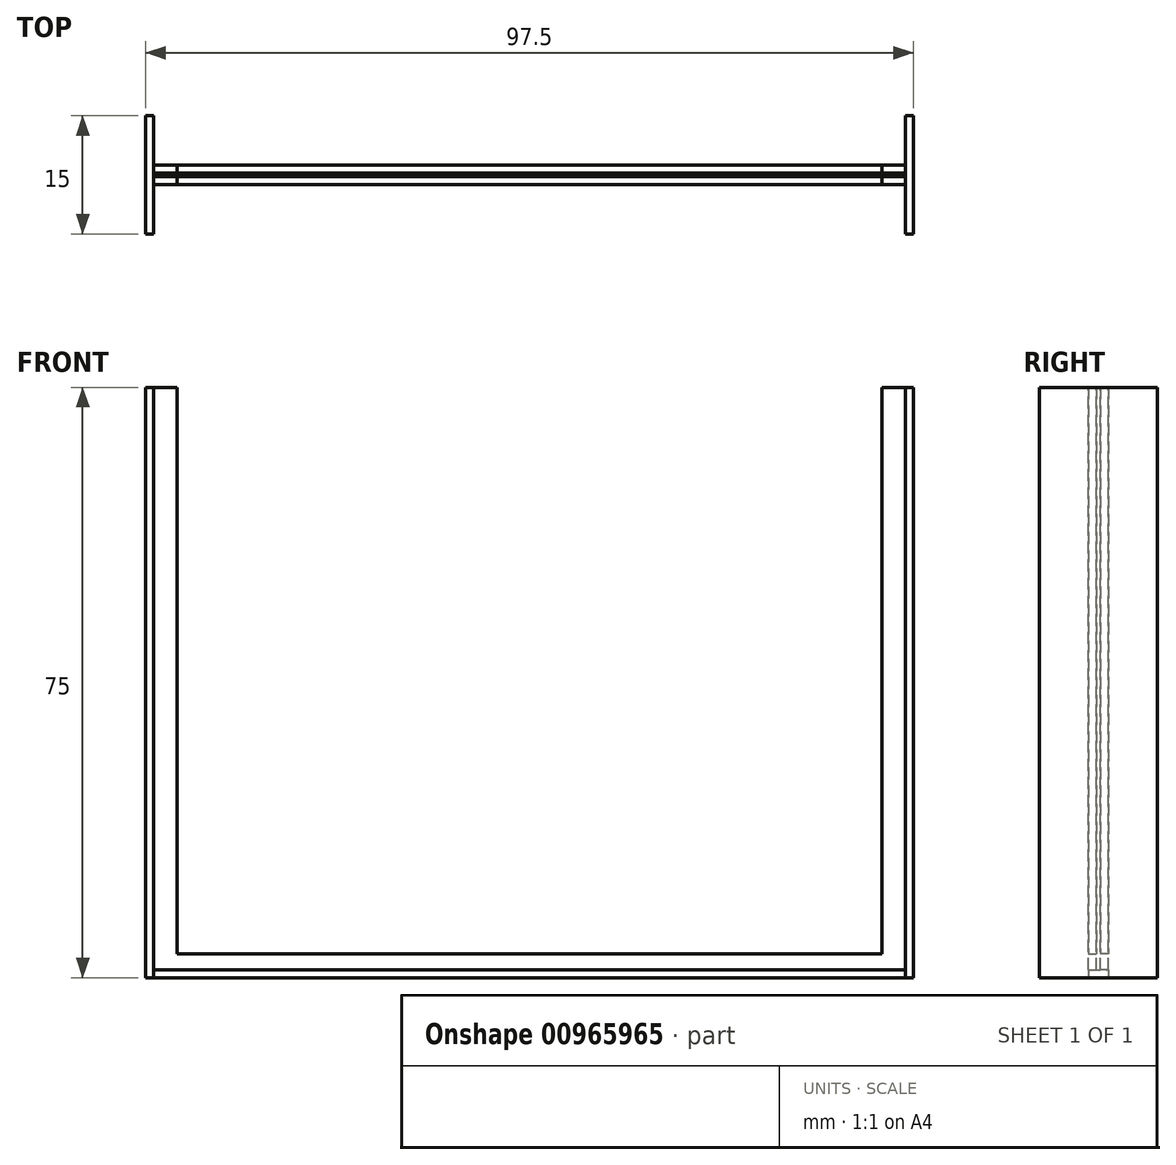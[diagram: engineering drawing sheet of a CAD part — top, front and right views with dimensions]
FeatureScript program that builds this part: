
annotation { "Feature Type Name" : "Feature", "Feature Type Description" : "" }
export const myFeature = defineFeature(function(context is Context, id is Id, definition is map)
    precondition{}
    {
        {
            var Q0;
            Q0=qCreatedBy(makeId("Front.planeOp"),FACE);
            var sketch = newSketch(context, id + "F0", { "sketchPlane" : qUnion([Q0])});
            skLineSegment(sketch, "E0", {"start": v(-47.75, 0) * mm, "end": v(47.75, 0) * mm});
            skLineSegment(sketch, "E1", {"start": v(47.75, 0) * mm, "end": v(47.75, 75) * mm});
            skLineSegment(sketch, "E2", {"start": v(-47.75, 75) * mm, "end": v(-47.75, 0) * mm});
            skLineSegment(sketch, "E3", {"start": v(47.75, 75) * mm, "end": v(48.75, 75) * mm});
            skLineSegment(sketch, "E4", {"start": v(48.75, 75) * mm, "end": v(48.75, 0) * mm});
            skLineSegment(sketch, "E5", {"start": v(48.75, 0) * mm, "end": v(47.75, 0) * mm});
            skLineSegment(sketch, "E6.MirrorCS", {"start": v(-48.75, 0) * mm, "end": v(-47.75, 0) * mm});
            skLineSegment(sketch, "E7.MirrorCS", {"start": v(-47.75, 75) * mm, "end": v(-48.75, 75) * mm});
            skLineSegment(sketch, "E8.MirrorCS", {"start": v(-48.75, 75) * mm, "end": v(-48.75, 0) * mm});
            skLineSegment(sketch, "E9", {"start": v(-44.75, 75) * mm, "end": v(-44.75, 3) * mm});
            skLineSegment(sketch, "E10", {"start": v(-44.75, 3) * mm, "end": v(0, 3) * mm});
            skLineSegment(sketch, "E11.MirrorCS", {"start": v(44.75, 75) * mm, "end": v(44.75, 3) * mm});
            skLineSegment(sketch, "E12.MirrorCS", {"start": v(44.75, 3) * mm, "end": v(0, 3) * mm});
            skLineSegment(sketch, "E13", {"start": v(-47.75, 75) * mm, "end": v(-44.75, 75) * mm});
            skLineSegment(sketch, "E14", {"start": v(44.75, 75) * mm, "end": v(47.75, 75) * mm});
            skLineSegment(sketch, "E15", {"start": v(-47.75, 1) * mm, "end": v(47.75, 1) * mm});
            skSolve(sketch);
        }
        {
            var Q0;
            Q0=makeQuery(id+"F0.imprint","IMPRINT",FACE,{"disambiguationData":[TD([[makeQuery(id+"F0.imprint","IMPRINT",EDGE,{"derivedFrom":sQuery(id+"F0.wireOp",EDGE,"E2")}),-1.0]])]});
            var Q1;
            Q1=makeQuery(id+"F0.imprint","IMPRINT",FACE,{"disambiguationData":[TD([[makeQuery(id+"F0.imprint","IMPRINT",EDGE,{"derivedFrom":sQuery(id+"F0.wireOp",EDGE,"E1")}),-1.0]])]});
            extrude(context, id + "F1", {"entities" : qUnion([Q0, Q1]), "endBound" : BoundingType.SYMMETRIC, "depth" : 15 * mm, "offsetDistance" : 25 * mm});
        }
        {
            var Q0;
            {var subQ0=sQuery(id+"F0.wireOp",EDGE,"E0");Q0=makeQuery(id+"F0.imprint","IMPRINT",FACE,{"disambiguationData":[TD([[makeQuery(id+"F0.imprint","IMPRINT",EDGE,{"derivedFrom":subQ0}),1.0]])]});}
            extrude(context, id + "F2", {"entities" : qUnion([Q0]), "endBound" : BoundingType.SYMMETRIC, "depth" : 2.5 * mm, "offsetDistance" : 25 * mm});
        }
        {
            var Q0;
            Q0=makeQuery(id+"F0.imprint","IMPRINT",FACE,{"disambiguationData":[TD([[makeQuery(id+"F0.imprint","IMPRINT",EDGE,{"derivedFrom":sQuery(id+"F0.wireOp",EDGE,"E9")}),-1.0]])]});
            extrude(context, id + "F3", {"entities" : qUnion([Q0]), "depth" : 1.25 * mm, "offsetDistance" : 25 * mm, "hasSecondDirection" : true, "secondDirectionOppositeDirection" : true, "secondDirectionDepth" : -0.25 * mm});
        }
        {
            var Q0;
            Q0=makeQuery(id+"F0.imprint","IMPRINT",FACE,{"disambiguationData":[TD([[makeQuery(id+"F0.imprint","IMPRINT",EDGE,{"derivedFrom":sQuery(id+"F0.wireOp",EDGE,"E9")}),-1.0]])]});
            extrude(context, id + "F4", {"entities" : qUnion([Q0]), "depth" : -1.25 * mm, "offsetDistance" : 25 * mm, "hasSecondDirection" : true, "secondDirectionOppositeDirection" : true, "secondDirectionDepth" : 0.25 * mm});
        }
    });
